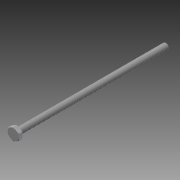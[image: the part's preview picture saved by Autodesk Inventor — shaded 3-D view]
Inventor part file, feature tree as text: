
AUTODESK INVENTOR PART (.ipt)
format: ipt  version: 2014 SP1 (Build 180222100, 222)  size: 1,693,696 bytes
history: native  units: in
note: dims shown in document units (in); Inventor stores cm internally (conversion verified against a paired STEP export)
features: extrude x1, other x1, imported_body x1
ambient origin geometry x8: Origin, YZ Plane, XZ Plane, XY Plane, X Axis, Y Axis, Z Axis, Center Point
bodies: Body1 (feature_tree)
feature tree (3):
  extrude  "Extrude14"  [1 undecoded]
  other  "92620A5591"
  imported_body  "Base1"
note: 1 required parameter value undecoded (feature->parameter linkage not recoverable at this tier; creation-order binding heuristic only, values carry confidence <= 0.55)
